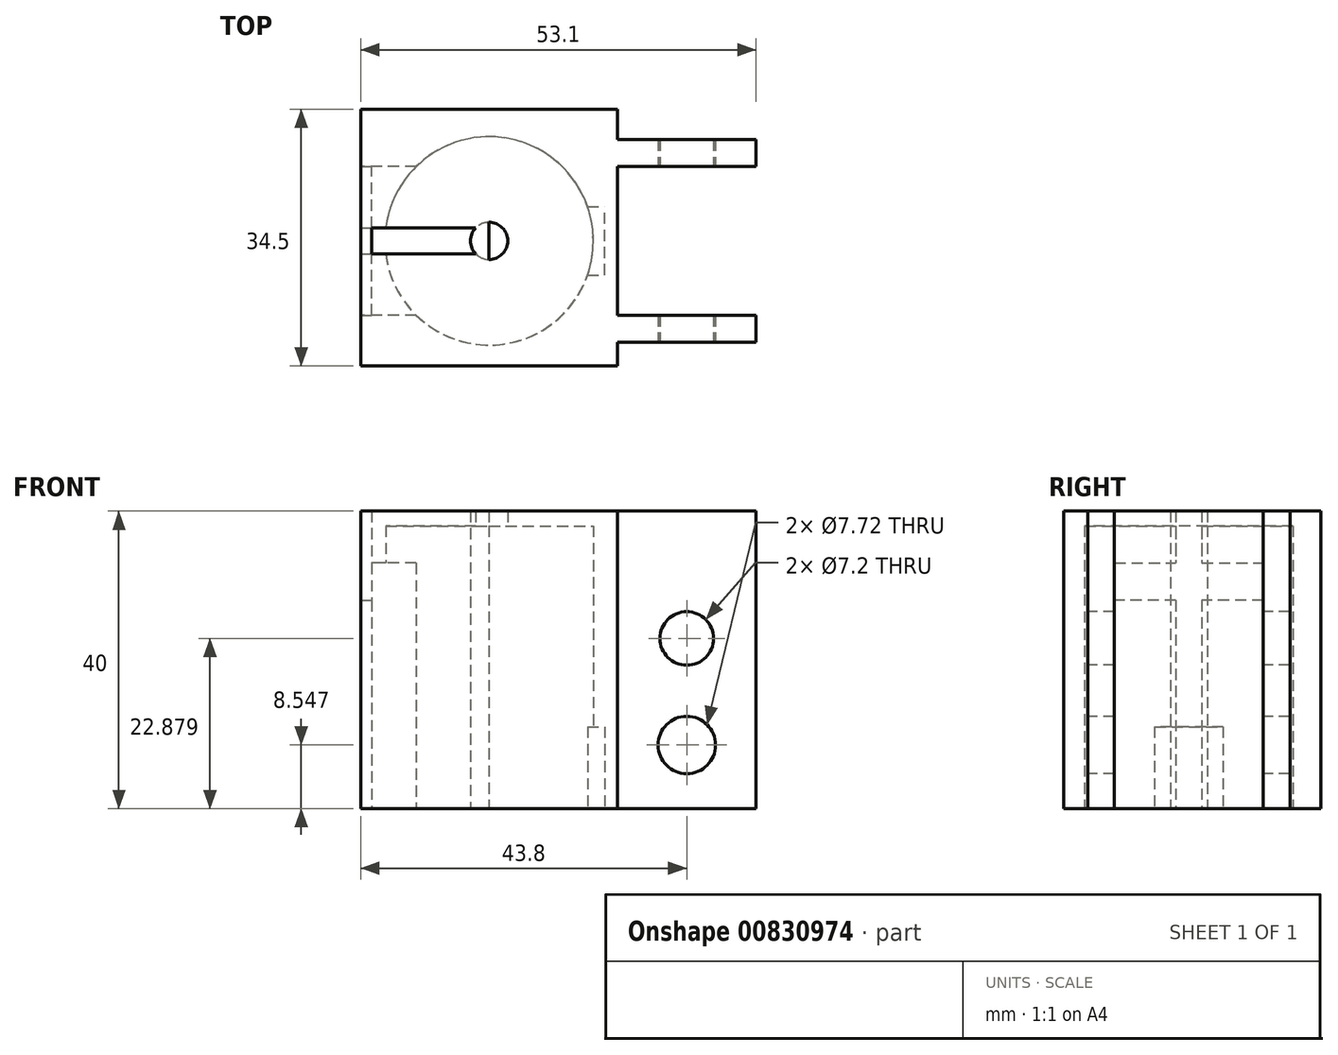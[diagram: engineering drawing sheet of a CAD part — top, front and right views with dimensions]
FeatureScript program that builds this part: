
annotation { "Feature Type Name" : "Feature", "Feature Type Description" : "" }
export const myFeature = defineFeature(function(context is Context, id is Id, definition is map)
    precondition{}
    {
        {
            var Q0;
            Q0=qCreatedBy(makeId("Top.planeOp"),FACE);
            var sketch = newSketch(context, id + "F0", { "sketchPlane" : qUnion([Q0])});
            skLineSegment(sketch, "E0.bottom", {"start": v(-17.25, 17.7) * mm, "end": v(17.25, 17.7) * mm});
            skLineSegment(sketch, "E0.top", {"start": v(-17.25, -16.8) * mm, "end": v(17.25, -16.8) * mm});
            skLineSegment(sketch, "E0.left", {"start": v(-17.25, 17.7) * mm, "end": v(-17.25, -16.8) * mm});
            skLineSegment(sketch, "E0.right", {"start": v(17.25, 17.7) * mm, "end": v(17.25, -16.8) * mm});
            skLineSegment(sketch, "E1.bottom", {"start": v(17.25, -10) * mm, "end": v(35.85, -10) * mm});
            skLineSegment(sketch, "E1.top", {"start": v(17.25, -13.6) * mm, "end": v(35.85, -13.6) * mm});
            skLineSegment(sketch, "E1.left", {"start": v(17.25, -10) * mm, "end": v(17.25, -13.6) * mm});
            skLineSegment(sketch, "E1.right", {"start": v(35.85, -10) * mm, "end": v(35.85, -13.6) * mm});
            skLineSegment(sketch, "E2.bottom", {"start": v(17.25, 13.6) * mm, "end": v(35.85, 13.6) * mm});
            skLineSegment(sketch, "E2.top", {"start": v(17.25, 10) * mm, "end": v(35.85, 10) * mm});
            skLineSegment(sketch, "E2.left", {"start": v(17.25, 13.6) * mm, "end": v(17.25, 10) * mm});
            skLineSegment(sketch, "E2.right", {"start": v(35.85, 13.6) * mm, "end": v(35.85, 10) * mm});
            skSolve(sketch);
        }
        {
            var Q0;
            Q0=makeQuery(id+"F0.imprint","IMPRINT",FACE,{"disambiguationData":[TD([[makeQuery(id+"F0.imprint","IMPRINT",EDGE,{"derivedFrom":sQuery(id+"F0.wireOp",EDGE,"E2.bottom")}),-1.0]])]});
            var Q1;
            {var subQ1=sQuery(id+"F0.wireOp",EDGE,"E0.bottom");Q1=makeQuery(id+"F0.imprint","IMPRINT",FACE,{"disambiguationData":[TD([[makeQuery(id+"F0.imprint","IMPRINT",EDGE,{"derivedFrom":subQ1}),-1.0]])]});}
            var Q2;
            Q2=makeQuery(id+"F0.imprint","IMPRINT",FACE,{"disambiguationData":[TD([[makeQuery(id+"F0.imprint","IMPRINT",EDGE,{"derivedFrom":sQuery(id+"F0.wireOp",EDGE,"E1.bottom")}),-1.0]])]});
            extrude(context, id + "F1", {"entities" : qUnion([Q0, Q1, Q2]), "depth" : 40 * mm, "offsetDistance" : 25 * mm});
        }
        {
            var Q0;
            Q0=makeQuery(id+"F1.opExtrude","CAP_FACE",FACE,{"disambiguationData":[OSD([sQuery(id+"F0.wireOp",EDGE,"E0.bottom"),sQuery(id+"F0.wireOp",EDGE,"E0.top"),sQuery(id+"F0.wireOp",EDGE,"E0.left"),sQuery(id+"F0.wireOp",EDGE,"E0.right"),sQuery(id+"F0.wireOp",EDGE,"E1.bottom"),sQuery(id+"F0.wireOp",EDGE,"E1.top"),sQuery(id+"F0.wireOp",EDGE,"E1.right"),sQuery(id+"F0.wireOp",EDGE,"E2.bottom"),sQuery(id+"F0.wireOp",EDGE,"E2.top"),sQuery(id+"F0.wireOp",EDGE,"E2.right")])],"isStart":true});
            var sketch = newSketch(context, id + "F2", { "sketchPlane" : qUnion([Q0])});
            skCircle(sketch, "E3", {"center": v(0, 0) * mm, "radius": 14 * mm});
            skLineSegment(sketch, "E4.bottom", {"start": v(0, 10) * mm, "end": v(-15.75, 10) * mm});
            skLineSegment(sketch, "E4.top", {"start": v(0, -10) * mm, "end": v(-15.75, -10) * mm});
            skLineSegment(sketch, "E4.left", {"start": v(0, 10) * mm, "end": v(0, -10) * mm});
            skLineSegment(sketch, "E4.right", {"start": v(-15.75, 10) * mm, "end": v(-15.75, -10) * mm});
            skLineSegment(sketch, "E5.bottom", {"start": v(-17.25, 10) * mm, "end": v(-15.75, 10) * mm});
            skLineSegment(sketch, "E5.top", {"start": v(-17.25, -10) * mm, "end": v(-15.75, -10) * mm});
            skLineSegment(sketch, "E5.left", {"start": v(-17.25, 10) * mm, "end": v(-17.25, -10) * mm});
            skLineSegment(sketch, "E6.bottom", {"start": v(0, 4.6) * mm, "end": v(15.55, 4.6) * mm});
            skLineSegment(sketch, "E6.top", {"start": v(0, -4.6) * mm, "end": v(15.55, -4.6) * mm});
            skLineSegment(sketch, "E6.left", {"start": v(0, 4.6) * mm, "end": v(0, -4.6) * mm});
            skLineSegment(sketch, "E6.right", {"start": v(15.55, 4.6) * mm, "end": v(15.55, -4.6) * mm});
            skLineSegment(sketch, "E7.bottom", {"start": v(-17.25, 1.75) * mm, "end": v(0, 1.75) * mm});
            skLineSegment(sketch, "E7.top", {"start": v(-17.25, -1.75) * mm, "end": v(0, -1.75) * mm});
            skLineSegment(sketch, "E7.left", {"start": v(-17.25, 1.75) * mm, "end": v(-17.25, -1.75) * mm});
            skLineSegment(sketch, "E7.right", {"start": v(0, 1.75) * mm, "end": v(0, -1.75) * mm});
            skCircle(sketch, "E8", {"center": v(0, 0) * mm, "radius": 2.5 * mm});
            skSolve(sketch);
        }
        {
            var Q0;
            {var subQ0=sQuery(id+"F2.wireOp",EDGE,"E7.right");Q0=makeQuery(id+"F2.imprint","IMPRINT",FACE,{"disambiguationData":[TD([[makeQuery(id+"F2.imprint","IMPRINT",EDGE,{"derivedFrom":subQ0}),1.0]])]});}
            var Q1;
            {var subQ1=sQuery(id+"F2.wireOp",EDGE,"E6.left");var subQ3=sQuery(id+"F2.wireOp",EDGE,"E8");var subQ4=makeQuery(id+"F2.imprint","INTERSECT",VERTEX,{"disambiguationData":[OD(0.0)],"derivedFrom":[subQ1,subQ3]});Q1=makeQuery(id+"F2.imprint","IMPRINT",FACE,{"disambiguationData":[TD([[makeQuery(id+"F2.imprint","IMPRINT",EDGE,{"disambiguationData":[TD([[subQ4,-1.0]])],"derivedFrom":subQ3}),1.0]])]});}
            var Q2;
            {var subQ1=sQuery(id+"F2.wireOp",EDGE,"E6.left");var subQ3=sQuery(id+"F2.wireOp",EDGE,"E8");var subQ4=makeQuery(id+"F2.imprint","INTERSECT",VERTEX,{"disambiguationData":[OD(1.0)],"derivedFrom":[subQ1,subQ3]});Q2=makeQuery(id+"F2.imprint","IMPRINT",FACE,{"disambiguationData":[TD([[makeQuery(id+"F2.imprint","IMPRINT",EDGE,{"disambiguationData":[TD([[subQ4,1.0]])],"derivedFrom":subQ3}),1.0]])]});}
            var Q3;
            {var subQ0=sQuery(id+"F2.wireOp",EDGE,"E7.right");Q3=makeQuery(id+"F2.imprint","IMPRINT",FACE,{"disambiguationData":[TD([[makeQuery(id+"F2.imprint","IMPRINT",EDGE,{"derivedFrom":subQ0}),-1.0]])]});}
            var Q4;
            {var subQ0=sQuery(id+"F2.wireOp",EDGE,"E7.bottom");var subQ1=sQuery(id+"F2.wireOp",EDGE,"E3");var subQ2=makeQuery(id+"F2.imprint","INTERSECT",VERTEX,{"derivedFrom":[subQ1,subQ0]});Q4=makeQuery(id+"F2.imprint","IMPRINT",FACE,{"disambiguationData":[TD([[makeQuery(id+"F2.imprint","IMPRINT",EDGE,{"disambiguationData":[TD([[subQ2,-1.0]])],"derivedFrom":subQ1}),1.0]])]});}
            var Q5;
            {var subQ0=sQuery(id+"F2.wireOp",EDGE,"E7.bottom");var subQ1=sQuery(id+"F2.wireOp",EDGE,"E3");var subQ2=makeQuery(id+"F2.imprint","INTERSECT",VERTEX,{"derivedFrom":[subQ1,subQ0]});Q5=makeQuery(id+"F2.imprint","IMPRINT",FACE,{"disambiguationData":[TD([[makeQuery(id+"F2.imprint","IMPRINT",EDGE,{"disambiguationData":[TD([[subQ2,-1.0]])],"derivedFrom":subQ1}),-1.0]])]});}
            var Q6;
            {var subQ5=sQuery(id+"F2.wireOp",EDGE,"E7.left");Q6=makeQuery(id+"F2.imprint","IMPRINT",FACE,{"disambiguationData":[TD([[makeQuery(id+"F2.imprint","IMPRINT",EDGE,{"derivedFrom":subQ5}),-1.0]])]});}
            extrude(context, id + "F3", {"entities" : qUnion([Q0, Q1, Q2, Q3, Q4, Q5, Q6]), "operationType" : NewBodyOperationType.REMOVE, "endBound" : BoundingType.UP_TO_NEXT, "oppositeDirection" : true, "depth" : 25 * mm, "offsetDistance" : 25 * mm});
        }
        {
            var Q0;
            {var subQ0=sQuery(id+"F2.wireOp",EDGE,"E4.top");var subQ1=sQuery(id+"F2.wireOp",EDGE,"E3");var subQ2=makeQuery(id+"F2.imprint","INTERSECT",VERTEX,{"derivedFrom":[subQ1,subQ0]});Q0=makeQuery(id+"F2.imprint","IMPRINT",FACE,{"disambiguationData":[TD([[makeQuery(id+"F2.imprint","IMPRINT",EDGE,{"disambiguationData":[TD([[subQ2,-1.0]])],"derivedFrom":subQ1}),1.0]])]});}
            var Q1;
            {var subQ0=sQuery(id+"F2.wireOp",EDGE,"E7.bottom");var subQ1=sQuery(id+"F2.wireOp",EDGE,"E3");var subQ2=makeQuery(id+"F2.imprint","INTERSECT",VERTEX,{"derivedFrom":[subQ1,subQ0]});Q1=makeQuery(id+"F2.imprint","IMPRINT",FACE,{"disambiguationData":[TD([[makeQuery(id+"F2.imprint","IMPRINT",EDGE,{"disambiguationData":[TD([[subQ2,-1.0]])],"derivedFrom":subQ1}),1.0]])]});}
            var Q2;
            {var subQ7=sQuery(id+"F2.wireOp",EDGE,"E3");var subQ9=sQuery(id+"F2.wireOp",EDGE,"E7.top");var subQ10=makeQuery(id+"F2.imprint","INTERSECT",VERTEX,{"derivedFrom":[subQ7,subQ9]});Q2=makeQuery(id+"F2.imprint","IMPRINT",FACE,{"disambiguationData":[TD([[makeQuery(id+"F2.imprint","IMPRINT",EDGE,{"disambiguationData":[TD([[subQ10,-1.0]])],"derivedFrom":subQ7}),1.0]])]});}
            var Q3;
            {var subQ5=sQuery(id+"F2.wireOp",EDGE,"E4.bottom");var subQ8=sQuery(id+"F2.wireOp",EDGE,"E3");var subQ11=makeQuery(id+"F2.imprint","INTERSECT",VERTEX,{"derivedFrom":[subQ8,subQ5]});Q3=makeQuery(id+"F2.imprint","IMPRINT",FACE,{"disambiguationData":[TD([[makeQuery(id+"F2.imprint","IMPRINT",EDGE,{"disambiguationData":[TD([[subQ11,-1.0]])],"derivedFrom":subQ8}),1.0]])]});}
            var Q4;
            {var subQ0=sQuery(id+"F2.wireOp",EDGE,"E4.bottom");var subQ1=sQuery(id+"F2.wireOp",EDGE,"E3");var subQ2=makeQuery(id+"F2.imprint","INTERSECT",VERTEX,{"derivedFrom":[subQ1,subQ0]});Q4=makeQuery(id+"F2.imprint","IMPRINT",FACE,{"disambiguationData":[TD([[makeQuery(id+"F2.imprint","IMPRINT",EDGE,{"disambiguationData":[TD([[subQ2,1.0]])],"derivedFrom":subQ1}),1.0]])]});}
            var Q5;
            {var subQ4=sQuery(id+"F2.wireOp",EDGE,"E3");var subQ6=sQuery(id+"F2.wireOp",EDGE,"E6.bottom");var subQ8=makeQuery(id+"F2.imprint","INTERSECT",VERTEX,{"derivedFrom":[subQ4,subQ6]});Q5=makeQuery(id+"F2.imprint","IMPRINT",FACE,{"disambiguationData":[TD([[makeQuery(id+"F2.imprint","IMPRINT",EDGE,{"disambiguationData":[TD([[subQ8,1.0]])],"derivedFrom":subQ4}),1.0]])]});}
            extrude(context, id + "F4", {"entities" : qUnion([Q0, Q1, Q2, Q3, Q4, Q5]), "operationType" : NewBodyOperationType.REMOVE, "oppositeDirection" : true, "depth" : 38 * mm, "offsetDistance" : 25 * mm});
        }
        {
            var Q0;
            {var subQ5=sQuery(id+"F2.wireOp",EDGE,"E6.right");Q0=makeQuery(id+"F2.imprint","IMPRINT",FACE,{"disambiguationData":[TD([[makeQuery(id+"F2.imprint","IMPRINT",EDGE,{"derivedFrom":subQ5}),-1.0]])]});}
            extrude(context, id + "F5", {"entities" : qUnion([Q0]), "operationType" : NewBodyOperationType.REMOVE, "oppositeDirection" : true, "depth" : 11 * mm, "offsetDistance" : 25 * mm});
        }
        {
            var Q0;
            {var subQ5=sQuery(id+"F2.wireOp",EDGE,"E4.bottom");var subQ7=sQuery(id+"F2.wireOp",EDGE,"E3");var subQ8=makeQuery(id+"F2.imprint","INTERSECT",VERTEX,{"derivedFrom":[subQ7,subQ5]});Q0=makeQuery(id+"F2.imprint","IMPRINT",FACE,{"disambiguationData":[TD([[makeQuery(id+"F2.imprint","IMPRINT",EDGE,{"disambiguationData":[TD([[subQ8,-1.0]])],"derivedFrom":subQ7}),-1.0]])]});}
            var Q1;
            {var subQ0=sQuery(id+"F2.wireOp",EDGE,"E7.bottom");var subQ1=sQuery(id+"F2.wireOp",EDGE,"E3");var subQ2=makeQuery(id+"F2.imprint","INTERSECT",VERTEX,{"derivedFrom":[subQ1,subQ0]});Q1=makeQuery(id+"F2.imprint","IMPRINT",FACE,{"disambiguationData":[TD([[makeQuery(id+"F2.imprint","IMPRINT",EDGE,{"disambiguationData":[TD([[subQ2,-1.0]])],"derivedFrom":subQ1}),-1.0]])]});}
            var Q2;
            {var subQ3=sQuery(id+"F2.wireOp",EDGE,"E7.top");var subQ7=sQuery(id+"F2.wireOp",EDGE,"E3");var subQ9=makeQuery(id+"F2.imprint","INTERSECT",VERTEX,{"derivedFrom":[subQ7,subQ3]});Q2=makeQuery(id+"F2.imprint","IMPRINT",FACE,{"disambiguationData":[TD([[makeQuery(id+"F2.imprint","IMPRINT",EDGE,{"disambiguationData":[TD([[subQ9,-1.0]])],"derivedFrom":subQ7}),-1.0]])]});}
            extrude(context, id + "F6", {"entities" : qUnion([Q0, Q1, Q2]), "operationType" : NewBodyOperationType.REMOVE, "oppositeDirection" : true, "depth" : 33 * mm, "offsetDistance" : 25 * mm});
        }
        {
            var Q0;
            {var subQ0=sQuery(id+"F2.wireOp",EDGE,"E5.bottom");Q0=makeQuery(id+"F2.imprint","IMPRINT",FACE,{"disambiguationData":[TD([[makeQuery(id+"F2.imprint","IMPRINT",EDGE,{"derivedFrom":subQ0}),-1.0]])]});}
            var Q1;
            {var subQ0=sQuery(id+"F2.wireOp",EDGE,"E5.top");Q1=makeQuery(id+"F2.imprint","IMPRINT",FACE,{"disambiguationData":[TD([[makeQuery(id+"F2.imprint","IMPRINT",EDGE,{"derivedFrom":subQ0}),1.0]])]});}
            extrude(context, id + "F7", {"entities" : qUnion([Q0, Q1]), "operationType" : NewBodyOperationType.REMOVE, "oppositeDirection" : true, "depth" : 28 * mm, "offsetDistance" : 25 * mm});
        }
        {
            var Q0;
            Q0=makeQuery(id+"F1.opExtrude","SWEPT_FACE",FACE,{"disambiguationData":[OSD([sQuery(id+"F0.wireOp",EDGE,"E1.top")])]});
            var sketch = newSketch(context, id + "F8", { "sketchPlane" : qUnion([Q0])});
            skCircle(sketch, "E9", {"center": v(26.55, 8.55) * mm, "radius": 3.86 * mm});
            skCircle(sketch, "E10", {"center": v(26.55, 22.88) * mm, "radius": 3.6 * mm});
            skSolve(sketch);
        }
        {
            var Q0;
            Q0=makeQuery(id+"F8.imprint","IMPRINT",FACE,{"disambiguationData":[TD([[makeQuery(id+"F8.imprint","IMPRINT",EDGE,{"derivedFrom":sQuery(id+"F8.wireOp",EDGE,"E9")}),1.0]])]});
            extrude(context, id + "F9", {"entities" : qUnion([Q0]), "operationType" : NewBodyOperationType.REMOVE, "oppositeDirection" : true, "depth" : 40000 * mm, "offsetDistance" : 25 * mm});
        }
        {
            var Q0;
            Q0=makeQuery(id+"F8.imprint","IMPRINT",FACE,{"disambiguationData":[TD([[makeQuery(id+"F8.imprint","IMPRINT",EDGE,{"derivedFrom":sQuery(id+"F8.wireOp",EDGE,"E10")}),1.0]])]});
            extrude(context, id + "F10", {"entities" : qUnion([Q0]), "operationType" : NewBodyOperationType.REMOVE, "oppositeDirection" : true, "depth" : 30 * mm, "offsetDistance" : 25 * mm});
        }
    });
